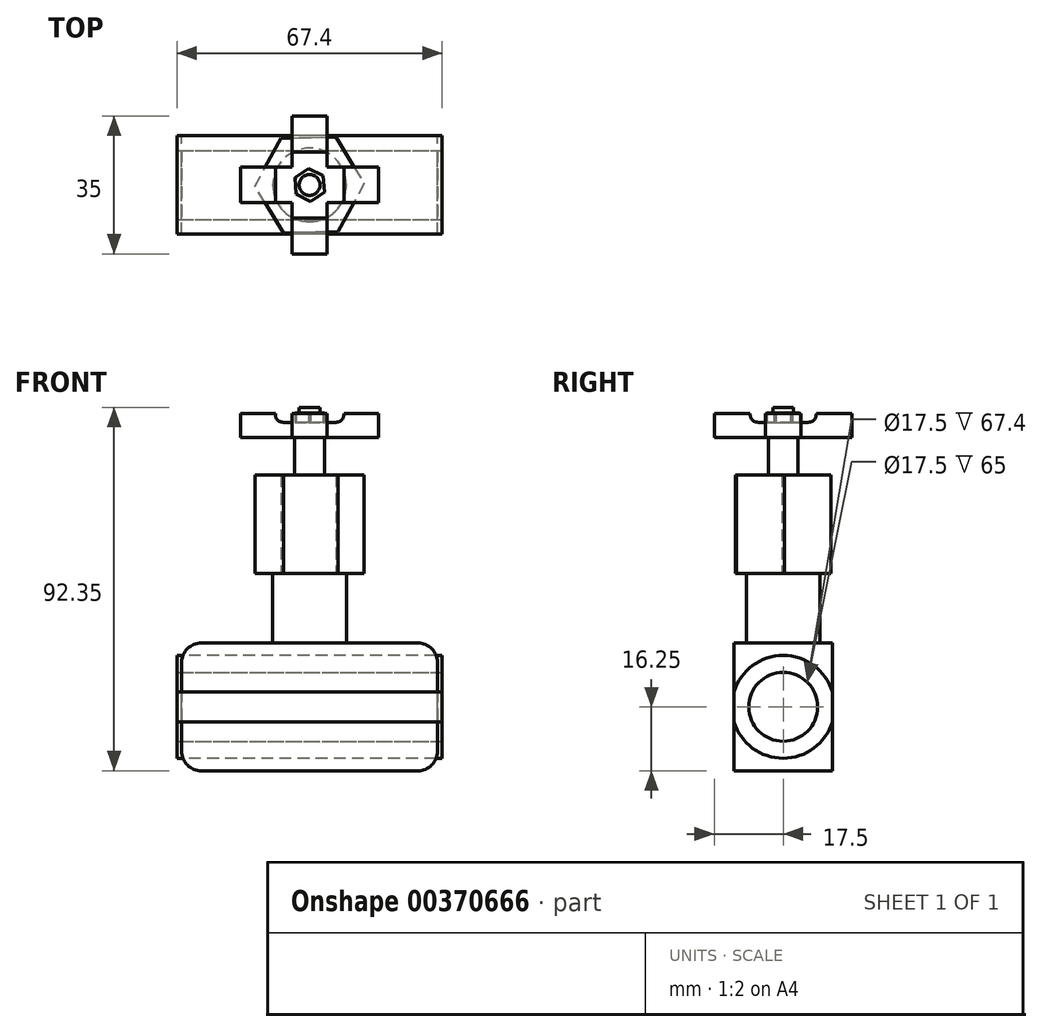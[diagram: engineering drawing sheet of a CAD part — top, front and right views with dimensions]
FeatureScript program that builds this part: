
annotation { "Feature Type Name" : "Feature", "Feature Type Description" : "" }
export const myFeature = defineFeature(function(context is Context, id is Id, definition is map)
    precondition{}
    {
        {
            var Q0;
            Q0=qCreatedBy(makeId("Front.planeOp"),FACE);
            var sketch = newSketch(context, id + "F0", { "sketchPlane" : qUnion([Q0])});
            skLineSegment(sketch, "E0.bottom", {"start": v(32.5, -16.25) * mm, "end": v(-32.5, -16.25) * mm});
            skLineSegment(sketch, "E0.top", {"start": v(32.5, 16.25) * mm, "end": v(-32.5, 16.25) * mm});
            skLineSegment(sketch, "E0.left", {"start": v(32.5, -16.25) * mm, "end": v(32.5, 16.25) * mm});
            skLineSegment(sketch, "E0.right", {"start": v(-32.5, -16.25) * mm, "end": v(-32.5, 16.25) * mm});
            skPoint(sketch, "E0.middle", {"position": v(0, 0) * mm});
            skSolve(sketch);
        }
        {
            var Q0;
            Q0=makeQuery(id+"F0.imprint","IMPRINT",FACE,{"disambiguationData":[TD([[makeQuery(id+"F0.imprint","IMPRINT",EDGE,{"derivedFrom":sQuery(id+"F0.wireOp",EDGE,"E0.bottom")}),-1.0]])]});
            extrude(context, id + "F1", {"entities" : qUnion([Q0]), "endBound" : BoundingType.SYMMETRIC, "depth" : 25 * mm});
        }
        {
            var Q0;
            Q0=qCreatedBy(makeId("Top.planeOp"),FACE);
            var sketch = newSketch(context, id + "F2", { "sketchPlane" : qUnion([Q0])});
            skCircle(sketch, "E1", {"center": v(0, 0) * mm, "radius": 9.35 * mm});
            skSolve(sketch);
        }
        {
            var Q0;
            Q0 = qSketchRegion(id + "F2", true);
            extrude(context, id + "F3", {"entities" : qUnion([Q0]), "operationType" : NewBodyOperationType.ADD, "depth" : 33.9 * mm});
        }
        {
            var Q0;
            Q0=makeQuery(id+"F1.opExtrude","SWEPT_EDGE",EDGE,{"disambiguationData":[OSD([sQuery(id+"F0.wireOp",EDGE,"E0.top"),sQuery(id+"F0.wireOp",EDGE,"E0.right")])]});
            var Q1;
            Q1=makeQuery(id+"F1.opExtrude","SWEPT_EDGE",EDGE,{"disambiguationData":[OSD([sQuery(id+"F0.wireOp",EDGE,"E0.bottom"),sQuery(id+"F0.wireOp",EDGE,"E0.right")])]});
            var Q2;
            Q2=makeQuery(id+"F1.opExtrude","SWEPT_EDGE",EDGE,{"disambiguationData":[OSD([sQuery(id+"F0.wireOp",EDGE,"E0.top"),sQuery(id+"F0.wireOp",EDGE,"E0.left")])]});
            var Q3;
            Q3=makeQuery(id+"F1.opExtrude","SWEPT_EDGE",EDGE,{"disambiguationData":[OSD([sQuery(id+"F0.wireOp",EDGE,"E0.bottom"),sQuery(id+"F0.wireOp",EDGE,"E0.left")])]});
            fillet(context, id + "F4", {"entities" : qUnion([Q0, Q1, Q2, Q3]), "radius" : 5 * mm, "tangentPropagation" : true, "allowEdgeOverflow" : false});
        }
        {
            var Q0;
            Q0=makeQuery(id+"F3.opExtrude","CAP_FACE",FACE,{"disambiguationData":[OSD([sQuery(id+"F2.wireOp",EDGE,"E1")])],"isStart":false});
            var sketch = newSketch(context, id + "F5", { "sketchPlane" : qUnion([Q0])});
            skCircle(sketch, "E2.cCircle", {"center": v(0, 0) * mm, "radius": 12.03 * mm, "construction": true});
            skLineSegment(sketch, "E2.0", {"start": v(-13.89, -0.31) * mm, "end": v(-7.22, 11.87) * mm});
            skLineSegment(sketch, "E2.1", {"start": v(-7.22, 11.87) * mm, "end": v(6.67, 12.19) * mm});
            skLineSegment(sketch, "E2.2", {"start": v(6.67, 12.19) * mm, "end": v(13.89, 0.31) * mm});
            skLineSegment(sketch, "E2.3", {"start": v(13.89, 0.31) * mm, "end": v(7.22, -11.87) * mm});
            skLineSegment(sketch, "E2.4", {"start": v(7.22, -11.87) * mm, "end": v(-6.67, -12.19) * mm});
            skLineSegment(sketch, "E2.5", {"start": v(-6.67, -12.19) * mm, "end": v(-13.89, -0.31) * mm});
            skPoint(sketch, "E2.0.midPoint", {"position": v(-10.55, 5.78) * mm});
            skSolve(sketch);
        }
        {
            var Q0;
            Q0 = qSketchRegion(id + "F5", true);
            extrude(context, id + "F6", {"entities" : qUnion([Q0]), "operationType" : NewBodyOperationType.ADD, "depth" : 25 * mm});
        }
        {
            var Q0;
            Q0=makeQuery(id+"F6.opExtrude","CAP_FACE",FACE,{"disambiguationData":[OSD([sQuery(id+"F5.wireOp",EDGE,"E2.0"),sQuery(id+"F5.wireOp",EDGE,"E2.1"),sQuery(id+"F5.wireOp",EDGE,"E2.2"),sQuery(id+"F5.wireOp",EDGE,"E2.3"),sQuery(id+"F5.wireOp",EDGE,"E2.4"),sQuery(id+"F5.wireOp",EDGE,"E2.5")])],"isStart":false});
            var sketch = newSketch(context, id + "F7", { "sketchPlane" : qUnion([Q0])});
            skCircle(sketch, "E3", {"center": v(0, 0) * mm, "radius": 3.8 * mm});
            skSolve(sketch);
        }
        {
            var Q0;
            Q0=makeQuery(id+"F7.imprint","IMPRINT",FACE,{"disambiguationData":[TD([[makeQuery(id+"F7.imprint","IMPRINT",EDGE,{"derivedFrom":sQuery(id+"F7.wireOp",EDGE,"E3")}),1.0]])]});
            extrude(context, id + "F8", {"entities" : qUnion([Q0]), "operationType" : NewBodyOperationType.ADD, "depth" : 9.6 * mm});
        }
        {
            var Q0;
            Q0=makeQuery(id+"F8.opExtrude","CAP_FACE",FACE,{"disambiguationData":[OSD([sQuery(id+"F7.wireOp",EDGE,"E3")])],"isStart":false});
            var sketch = newSketch(context, id + "F9", { "sketchPlane" : qUnion([Q0])});
            skLineSegment(sketch, "E4.bottom", {"start": v(4.5, 17.5) * mm, "end": v(-4.5, 17.5) * mm});
            skLineSegment(sketch, "E4.top", {"start": v(4.5, -17.5) * mm, "end": v(-4.5, -17.5) * mm});
            skLineSegment(sketch, "E4.left", {"start": v(4.5, 17.5) * mm, "end": v(4.5, -17.5) * mm});
            skLineSegment(sketch, "E4.right", {"start": v(-4.5, 17.5) * mm, "end": v(-4.5, -17.5) * mm});
            skPoint(sketch, "E4.middle", {"position": v(0, 0) * mm});
            skSolve(sketch);
        }
        {
            var Q0;
            Q0=makeQuery(id+"F9.imprint","IMPRINT",FACE,{"disambiguationData":[TD([[makeQuery(id+"F9.imprint","IMPRINT",EDGE,{"derivedFrom":makeQuery(id+"F8.opExtrude","CAP_EDGE",EDGE,{"disambiguationData":[OSD([sQuery(id+"F7.wireOp",EDGE,"E3")])],"isStart":false})}),1.0]])]});
            var sketch = newSketch(context, id + "F10", { "sketchPlane" : qUnion([Q0])});
            skLineSegment(sketch, "E5.bottom", {"start": v(-17.5, 4.5) * mm, "end": v(17.5, 4.5) * mm});
            skLineSegment(sketch, "E5.top", {"start": v(-17.5, -4.5) * mm, "end": v(17.5, -4.5) * mm});
            skLineSegment(sketch, "E5.left", {"start": v(-17.5, 4.5) * mm, "end": v(-17.5, -4.5) * mm});
            skLineSegment(sketch, "E5.right", {"start": v(17.5, 4.5) * mm, "end": v(17.5, -4.5) * mm});
            skPoint(sketch, "E5.middle", {"position": v(0, 0) * mm});
            skSolve(sketch);
        }
        {
            var Q0;
            Q0=makeQuery(id+"F10.imprint","IMPRINT",FACE,{"disambiguationData":[TD([[makeQuery(id+"F10.imprint","IMPRINT",EDGE,{"derivedFrom":sQuery(id+"F10.wireOp",EDGE,"E5.bottom")}),-1.0]])]});
            extrude(context, id + "F11", {"entities" : qUnion([Q0]), "depth" : 6 * mm});
        }
        {
            var Q0;
            Q0=makeQuery(id+"F9.imprint","IMPRINT",FACE,{"disambiguationData":[TD([[makeQuery(id+"F9.imprint","IMPRINT",EDGE,{"derivedFrom":sQuery(id+"F9.wireOp",EDGE,"E4.bottom")}),1.0]])]});
            extrude(context, id + "F12", {"entities" : qUnion([Q0]), "operationType" : NewBodyOperationType.ADD, "depth" : 6 * mm});
        }
        {
            var Q0;
            {var subQ0=sQuery(id+"F7.wireOp",EDGE,"E3");Q0=makeQuery(id+"F12.boolean.opBoolean","MERGE",FACE,{"derivedFrom":[makeQuery(id+"F11.opExtrude","CAP_FACE",FACE,{"disambiguationData":[OSD([subQ0,sQuery(id+"F10.wireOp",EDGE,"E5.bottom"),sQuery(id+"F10.wireOp",EDGE,"E5.top"),sQuery(id+"F10.wireOp",EDGE,"E5.left"),sQuery(id+"F10.wireOp",EDGE,"E5.right")])],"isStart":false}),makeQuery(id+"F12.opExtrude","CAP_FACE",FACE,{"disambiguationData":[OSD([subQ0,sQuery(id+"F9.wireOp",EDGE,"E4.bottom"),sQuery(id+"F9.wireOp",EDGE,"E4.top"),sQuery(id+"F9.wireOp",EDGE,"E4.left"),sQuery(id+"F9.wireOp",EDGE,"E4.right")])],"isStart":false})]});}
            var sketch = newSketch(context, id + "F13", { "sketchPlane" : qUnion([Q0])});
            skPoint(sketch, "E6.middle", {"position": v(0, 0) * mm});
            skSolve(sketch);
        }
        {
            var Q0;
            Q0=makeQuery(id+"F13.imprint","IMPRINT",FACE,{"disambiguationData":[TD([[makeQuery(id+"F13.imprint","IMPRINT",EDGE,{"derivedFrom":makeQuery(id+"F11.opExtrude","CAP_EDGE",EDGE,{"disambiguationData":[OSD([sQuery(id+"F7.wireOp",EDGE,"E3")])],"isStart":false})}),1.0]])]});
            extrude(context, id + "F14", {"entities" : qUnion([Q0]), "operationType" : NewBodyOperationType.ADD, "oppositeDirection" : true, "depth" : 15.4 * mm});
        }
        {
            var Q0;
            {var subQ0=sQuery(id+"F7.wireOp",EDGE,"E3");Q0=makeQuery(id+"F14.boolean.opBoolean","MERGE",FACE,{"derivedFrom":[makeQuery(id+"F12.boolean.opBoolean","MERGE",FACE,{"derivedFrom":[makeQuery(id+"F11.opExtrude","CAP_FACE",FACE,{"disambiguationData":[OSD([subQ0,sQuery(id+"F10.wireOp",EDGE,"E5.bottom"),sQuery(id+"F10.wireOp",EDGE,"E5.top"),sQuery(id+"F10.wireOp",EDGE,"E5.left"),sQuery(id+"F10.wireOp",EDGE,"E5.right")])],"isStart":false}),makeQuery(id+"F12.opExtrude","CAP_FACE",FACE,{"disambiguationData":[OSD([subQ0,sQuery(id+"F9.wireOp",EDGE,"E4.bottom"),sQuery(id+"F9.wireOp",EDGE,"E4.top"),sQuery(id+"F9.wireOp",EDGE,"E4.left"),sQuery(id+"F9.wireOp",EDGE,"E4.right")])],"isStart":false})]}),makeQuery(id+"F14.opExtrude","CAP_FACE",FACE,{"disambiguationData":[OSD([subQ0])],"isStart":true})]});}
            var sketch = newSketch(context, id + "F15", { "sketchPlane" : qUnion([Q0])});
            skLineSegment(sketch, "E7.bottom", {"start": v(8.71, -8.4) * mm, "end": v(-8.71, -8.4) * mm});
            skLineSegment(sketch, "E7.top", {"start": v(8.71, 8.4) * mm, "end": v(-8.71, 8.4) * mm});
            skLineSegment(sketch, "E7.left", {"start": v(8.71, -8.4) * mm, "end": v(8.71, 8.4) * mm});
            skLineSegment(sketch, "E7.right", {"start": v(-8.71, -8.4) * mm, "end": v(-8.71, 8.4) * mm});
            skPoint(sketch, "E7.middle", {"position": v(0, 0) * mm});
            skSolve(sketch);
        }
        {
            var Q0;
            {var subQ3=sQuery(id+"F9.wireOp",EDGE,"E4.left");var subQ7=sQuery(id+"F10.wireOp",EDGE,"E5.top");var subQ8=makeQuery(id+"F11.opExtrude","SWEPT_FACE",FACE,{"disambiguationData":[OSD([subQ7])]});var subQ14=makeQuery(id+"F12.opExtrude","CAP_EDGE",EDGE,{"disambiguationData":[OSD([subQ3])],"isStart":false});var subQ15=makeQuery(id+"F12.boolean.opBoolean","SPLIT",EDGE,{"disambiguationData":[TD([subQ8])],"derivedFrom":subQ14});var subQ20=sQuery(id+"F15.wireOp",EDGE,"E7.bottom");var subQ21=makeQuery(id+"F15.imprint","INTERSECT",VERTEX,{"derivedFrom":[subQ15,subQ20]});Q0=makeQuery(id+"F15.imprint","IMPRINT",FACE,{"disambiguationData":[TD([[makeQuery(id+"F15.imprint","IMPRINT",EDGE,{"disambiguationData":[TD([[subQ21,-1.0]])],"derivedFrom":subQ20}),-1.0]])]});}
            extrude(context, id + "F16", {"entities" : qUnion([Q0]), "operationType" : NewBodyOperationType.REMOVE, "oppositeDirection" : true, "depth" : 2.2 * mm});
        }
        {
            var Q0;
            Q0=makeQuery(id+"F16.boolean.opBoolean","COPY",EDGE,{"derivedFrom":makeQuery(id+"F16.opExtrude","CAP_EDGE",EDGE,{"disambiguationData":[OSD([sQuery(id+"F15.wireOp",EDGE,"E7.left")])],"isStart":false})});
            var Q1;
            Q1=makeQuery(id+"F16.boolean.opBoolean","COPY",EDGE,{"derivedFrom":makeQuery(id+"F16.opExtrude","CAP_EDGE",EDGE,{"disambiguationData":[OSD([sQuery(id+"F15.wireOp",EDGE,"E7.top")])],"isStart":false})});
            var Q2;
            Q2=makeQuery(id+"F16.boolean.opBoolean","COPY",EDGE,{"derivedFrom":makeQuery(id+"F16.opExtrude","CAP_EDGE",EDGE,{"disambiguationData":[OSD([sQuery(id+"F15.wireOp",EDGE,"E7.right")])],"isStart":false})});
            var Q3;
            Q3=makeQuery(id+"F16.boolean.opBoolean","COPY",EDGE,{"derivedFrom":makeQuery(id+"F16.opExtrude","CAP_EDGE",EDGE,{"disambiguationData":[OSD([sQuery(id+"F15.wireOp",EDGE,"E7.bottom")])],"isStart":false})});
            fillet(context, id + "F17", {"entities" : qUnion([Q0, Q1, Q2, Q3]), "radius" : 2 * mm, "tangentPropagation" : true, "allowEdgeOverflow" : false});
        }
        {
            var Q0;
            Q0=makeQuery(id+"F16.boolean.opBoolean","COPY",FACE,{"derivedFrom":makeQuery(id+"F16.opExtrude","CAP_FACE",FACE,{"disambiguationData":[OSD([sQuery(id+"F9.wireOp",EDGE,"E4.left"),sQuery(id+"F9.wireOp",EDGE,"E4.right"),sQuery(id+"F10.wireOp",EDGE,"E5.bottom"),sQuery(id+"F10.wireOp",EDGE,"E5.top"),sQuery(id+"F15.wireOp",EDGE,"E7.bottom"),sQuery(id+"F15.wireOp",EDGE,"E7.top"),sQuery(id+"F15.wireOp",EDGE,"E7.left"),sQuery(id+"F15.wireOp",EDGE,"E7.right")])],"isStart":false})});
            var sketch = newSketch(context, id + "F18", { "sketchPlane" : qUnion([Q0])});
            skCircle(sketch, "E8.cCircle", {"center": v(0, 0) * mm, "radius": 3.62 * mm, "construction": true});
            skLineSegment(sketch, "E8.0", {"start": v(0.3, -4.17) * mm, "end": v(-3.46, -2.33) * mm});
            skLineSegment(sketch, "E8.1", {"start": v(-3.46, -2.33) * mm, "end": v(-3.75, 1.83) * mm});
            skLineSegment(sketch, "E8.2", {"start": v(-3.75, 1.83) * mm, "end": v(-0.3, 4.17) * mm});
            skLineSegment(sketch, "E8.3", {"start": v(-0.3, 4.17) * mm, "end": v(3.46, 2.33) * mm});
            skLineSegment(sketch, "E8.4", {"start": v(3.46, 2.33) * mm, "end": v(3.75, -1.83) * mm});
            skLineSegment(sketch, "E8.5", {"start": v(3.75, -1.83) * mm, "end": v(0.3, -4.17) * mm});
            skPoint(sketch, "E8.0.midPoint", {"position": v(-1.59, -3.25) * mm});
            skSolve(sketch);
        }
        {
            var Q0;
            Q0=makeQuery(id+"F18.imprint","IMPRINT",FACE,{"disambiguationData":[TD([[makeQuery(id+"F18.imprint","IMPRINT",EDGE,{"derivedFrom":sQuery(id+"F18.wireOp",EDGE,"E8.0")}),-1.0]])]});
            extrude(context, id + "F19", {"entities" : qUnion([Q0]), "operationType" : NewBodyOperationType.ADD, "depth" : 2.3 * mm});
        }
        {
            var Q0;
            Q0=makeQuery(id+"F19.opExtrude","CAP_FACE",FACE,{"disambiguationData":[OSD([sQuery(id+"F18.wireOp",EDGE,"E8.0"),sQuery(id+"F18.wireOp",EDGE,"E8.1"),sQuery(id+"F18.wireOp",EDGE,"E8.2"),sQuery(id+"F18.wireOp",EDGE,"E8.3"),sQuery(id+"F18.wireOp",EDGE,"E8.4"),sQuery(id+"F18.wireOp",EDGE,"E8.5")])],"isStart":false});
            var sketch = newSketch(context, id + "F20", { "sketchPlane" : qUnion([Q0])});
            skCircle(sketch, "E9", {"center": v(0, 0) * mm, "radius": 2.65 * mm});
            skSolve(sketch);
        }
        {
            var Q0;
            Q0=makeQuery(id+"F20.imprint","IMPRINT",FACE,{"disambiguationData":[TD([[makeQuery(id+"F20.imprint","IMPRINT",EDGE,{"derivedFrom":sQuery(id+"F20.wireOp",EDGE,"E9")}),1.0]])]});
            extrude(context, id + "F21", {"entities" : qUnion([Q0]), "operationType" : NewBodyOperationType.ADD, "depth" : 1.5 * mm});
        }
        {
            var Q0;
            Q0=qCreatedBy(makeId("Right.planeOp"),FACE);
            var sketch = newSketch(context, id + "F22", { "sketchPlane" : qUnion([Q0])});
            skArc(sketch, "E10", {"start": v(-12.5, -3.8) * mm, "mid": v(0, -13.07) * mm, "end": v(12.5, -3.78) * mm});
            skLineSegment(sketch, "E11", {"start": v(-12.5, 3.8) * mm, "end": v(-12.5, -3.8) * mm});
            skLineSegment(sketch, "E12", {"start": v(12.5, 3.78) * mm, "end": v(12.5, -3.78) * mm});
            skArc(sketch, "E13.trimOffspring", {"start": v(12.5, 3.78) * mm, "mid": v(0, 13.07) * mm, "end": v(-12.5, 3.8) * mm});
            skSolve(sketch);
        }
        {
            var Q0;
            Q0 = qSketchRegion(id + "F22", true);
            extrude(context, id + "F23", {"entities" : qUnion([Q0]), "endBound" : BoundingType.SYMMETRIC, "depth" : 67.4 * mm});
        }
        {
            var Q0;
            Q0=makeQuery(id+"F23.opExtrude","CAP_FACE",FACE,{"disambiguationData":[OSD([sQuery(id+"F22.wireOp",EDGE,"E10")])],"isStart":false});
            var sketch = newSketch(context, id + "F24", { "sketchPlane" : qUnion([Q0])});
            skCircle(sketch, "E14", {"center": v(0, 0) * mm, "radius": 9.5 * mm});
            skSolve(sketch);
        }
        {
            var Q0;
            Q0=sQuery(id+"F24.wireOp",VERTEX,"E14.center");
            var Q1;
            Q1=makeQuery(id+"F1.opExtrude","SWEPT_BODY",BODY,{"disambiguationData":[OSD([sQuery(id+"F0.wireOp",EDGE,"E0.bottom"),sQuery(id+"F0.wireOp",EDGE,"E0.top"),sQuery(id+"F0.wireOp",EDGE,"E0.left"),sQuery(id+"F0.wireOp",EDGE,"E0.right")])]});
            var Q2;
            Q2=makeQuery(id+"F23.opExtrude","SWEPT_BODY",BODY,{"disambiguationData":[OSD([sQuery(id+"F22.wireOp",EDGE,"E10")])]});
            hole(context, id + "F25", {"style" : HoleStyle.SIMPLE, "endStyle" : HoleEndStyle.THROUGH, "holeDiameter" : 17.5 * mm, "isTappedThrough" : true, "tappedDepth" : 12 * mm, "tapClearance" : 3, "locations" : qUnion([Q0]), "scope" : qUnion([Q1, Q2])});
        }
    });
